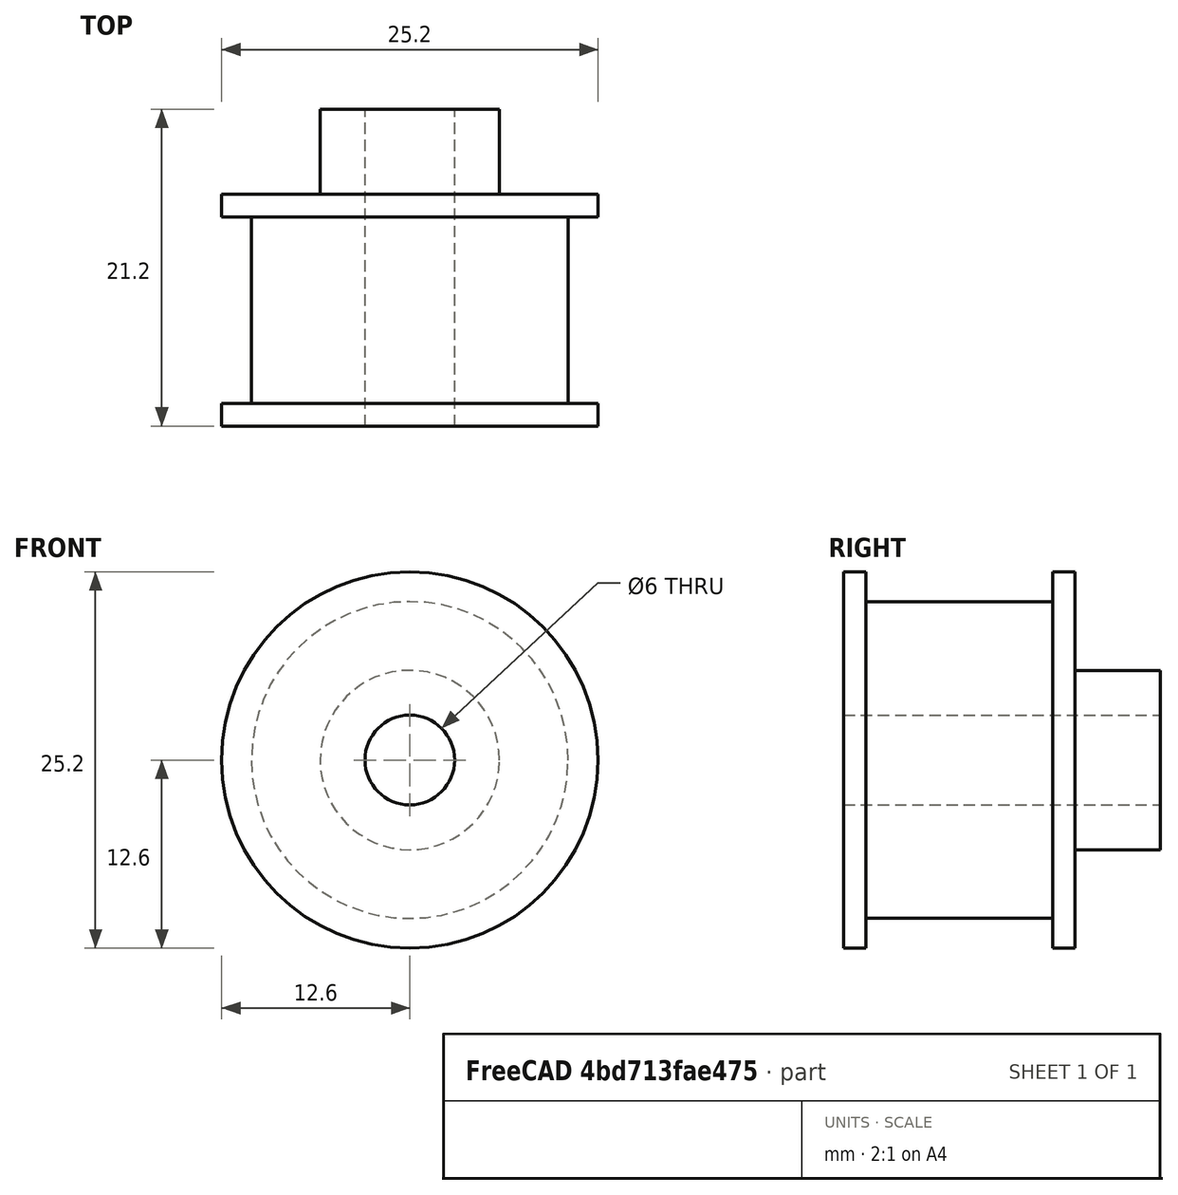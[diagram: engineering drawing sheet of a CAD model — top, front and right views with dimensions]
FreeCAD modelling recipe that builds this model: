
FCSTD DOCUMENT  (FreeCAD 0.15R4669 (Git))
Label: BR_petitePoulie
License: All rights reserved
LicenseURL: http://en.wikipedia.org/wiki/All_rights_reserved
objects: Sketcher::SketchObject×1, Part::Revolution×1
note: 2 computed .brp shape members not serialized (recipe doc carries the construction recipe); baked Part::Feature solids carry a one-line shape summary decoded from their .brp

FEATURE [Sketcher::SketchObject] Sketch  label="coupePetitePoulie"
  sketch-geometry (10):
    g0: LineSegment StartX=3 StartY=-10.6 StartZ=0 EndX=3 EndY=10.6 EndZ=0
    g1: LineSegment StartX=3 StartY=10.6 StartZ=0 EndX=6 EndY=10.6 EndZ=0
    g2: LineSegment StartX=6 StartY=10.6 StartZ=0 EndX=6 EndY=4.9 EndZ=0
    g3: LineSegment StartX=6 StartY=4.9 StartZ=0 EndX=12.6 EndY=4.9 EndZ=0
    g4: LineSegment StartX=12.6 StartY=4.9 StartZ=0 EndX=12.6 EndY=3.4 EndZ=0
    g5: LineSegment StartX=12.6 StartY=3.4 StartZ=0 EndX=10.6 EndY=3.4 EndZ=0
    g6: LineSegment StartX=10.6 StartY=3.4 StartZ=0 EndX=10.6 EndY=-9.1 EndZ=0
    g7: LineSegment StartX=10.6 StartY=-9.1 StartZ=0 EndX=12.6 EndY=-9.1 EndZ=0
    g8: LineSegment StartX=12.6 StartY=-9.1 StartZ=0 EndX=12.6 EndY=-10.6 EndZ=0
    g9: LineSegment StartX=12.6 StartY=-10.6 StartZ=0 EndX=3 EndY=-10.6 EndZ=0
  constraints (30):
    c: Vertical(g0)
    c: Coincident(g1,g0)
    c: Horizontal(g1)
    c: Coincident(g2,g1)
    c: Vertical(g2)
    c: Coincident(g3,g2)
    c: Horizontal(g3)
    c: Coincident(g4,g3)
    c: Vertical(g4)
    c: Coincident(g5,g4)
    c: Horizontal(g5)
    c: Coincident(g6,g5)
    c: Vertical(g6)
    c: Coincident(g7,g6)
    c: Horizontal(g7)
    c: Coincident(g8,g7)
    c: Vertical(g8)
    c: Coincident(g9,g8)
    c: Coincident(g9,g0)
    c: Horizontal(g9)
    c: PointOnObject(g4,g8)
    c: DistanceX(g-1,g0) = 3
    c: DistanceX(g-1,g1) = 6
    c: DistanceY(g3,g8) = -15.5
    c: DistanceY(g0,g0) = 21.2
    c: Symmetric(g0,g0,g-1)
    c: DistanceY(g6) = -12.5
    c: DistanceX(g-1,g5) = 10.6
    c: DistanceX(g-1,g8) = 12.6
    c: DistanceY(g8) = -1.5
FEATURE [Part::Revolution] Revolve  label="petitePoulie"
  Angle = 360
  Axis = (0,1,0)
  Base = (0,0,0)
  Solid = true
  Source = -> Sketch
